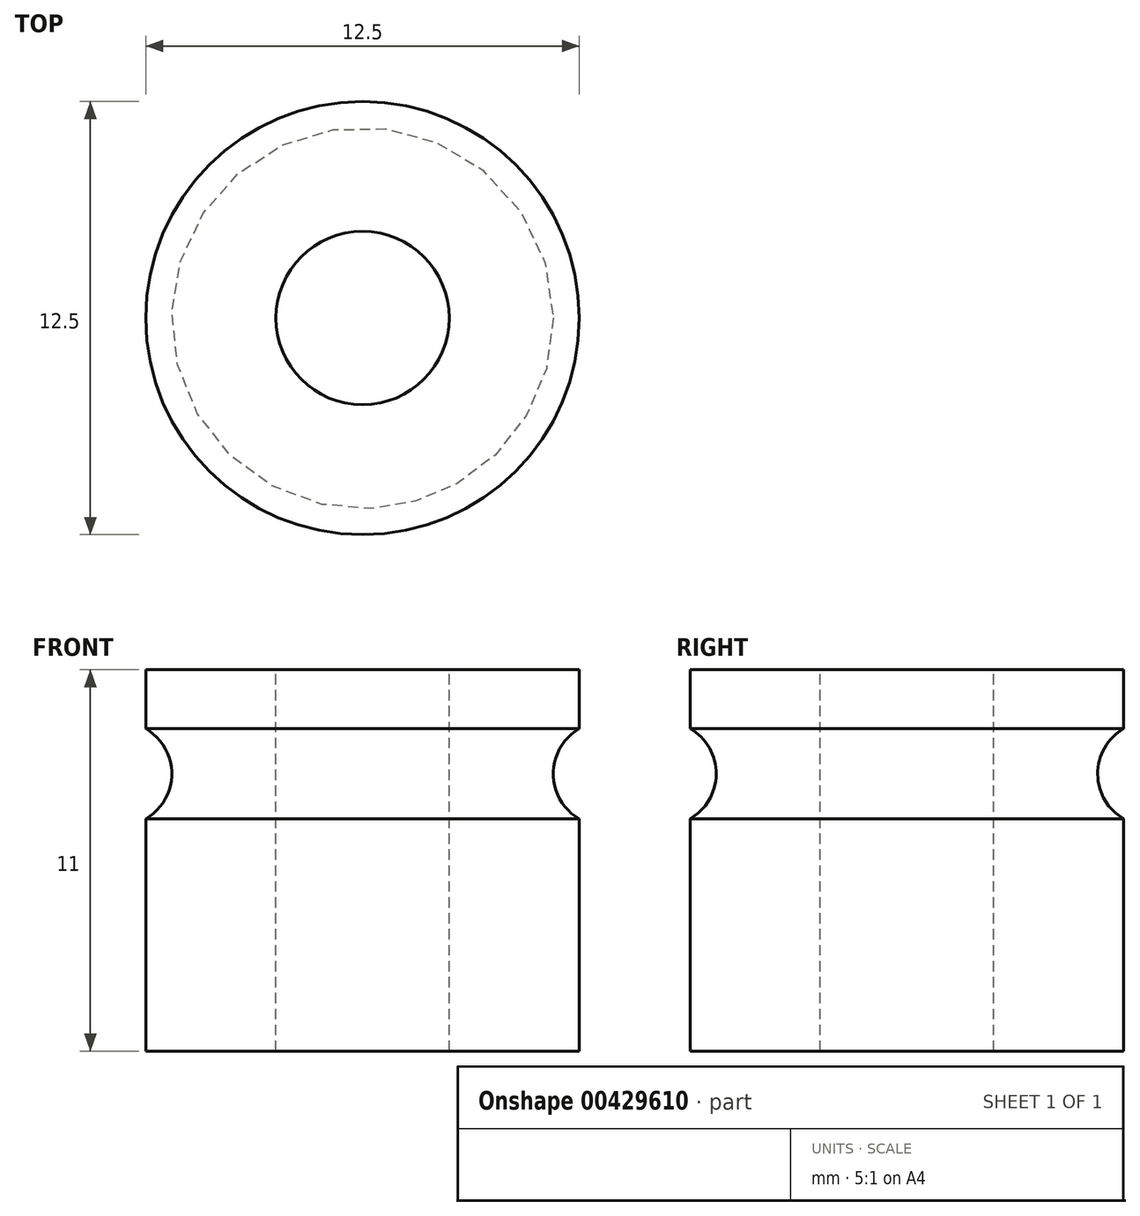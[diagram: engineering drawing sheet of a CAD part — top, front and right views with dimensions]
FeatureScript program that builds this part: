
annotation { "Feature Type Name" : "Feature", "Feature Type Description" : "" }
export const myFeature = defineFeature(function(context is Context, id is Id, definition is map)
    precondition{}
    {
        {
            var Q0;
            Q0=qCreatedBy(makeId("Front.planeOp"),FACE);
            var sketch = newSketch(context, id + "F0", { "sketchPlane" : qUnion([Q0])});
            skLineSegment(sketch, "E0", {"start": v(-2.5, 0) * mm, "end": v(-6.25, 0) * mm});
            skLineSegment(sketch, "E1", {"start": v(-6.25, 0) * mm, "end": v(-6.25, 6.7) * mm});
            skLineSegment(sketch, "E2", {"start": v(-6.25, 9.3) * mm, "end": v(-6.25, 11) * mm});
            skLineSegment(sketch, "E3", {"start": v(-6.25, 11) * mm, "end": v(-2.5, 11) * mm});
            skLineSegment(sketch, "E4", {"start": v(0, 11) * mm, "end": v(0, 0) * mm, "construction": true});
            skArc(sketch, "E5", {"start": v(-6.25, 6.7) * mm, "mid": v(-5.5, 8) * mm, "end": v(-6.25, 9.3) * mm});
            skLineSegment(sketch, "E6", {"start": v(-2.5, 11) * mm, "end": v(-2.5, 0) * mm});
            skSolve(sketch);
        }
        {
            var Q0;
            Q0=makeQuery(id+"F0.imprint","IMPRINT",FACE,{"disambiguationData":[TD([[makeQuery(id+"F0.imprint","IMPRINT",EDGE,{"derivedFrom":sQuery(id+"F0.wireOp",EDGE,"E0")}),-1.0]])]});
            var Q1;
            Q1=sQuery(id+"F0.wireOp",EDGE,"E4");
            revolve(context, id + "F1", {"entities" : qUnion([Q0]), "axis" : qUnion([Q1]), "revolveType" : RevolveType.FULL});
        }
    });
